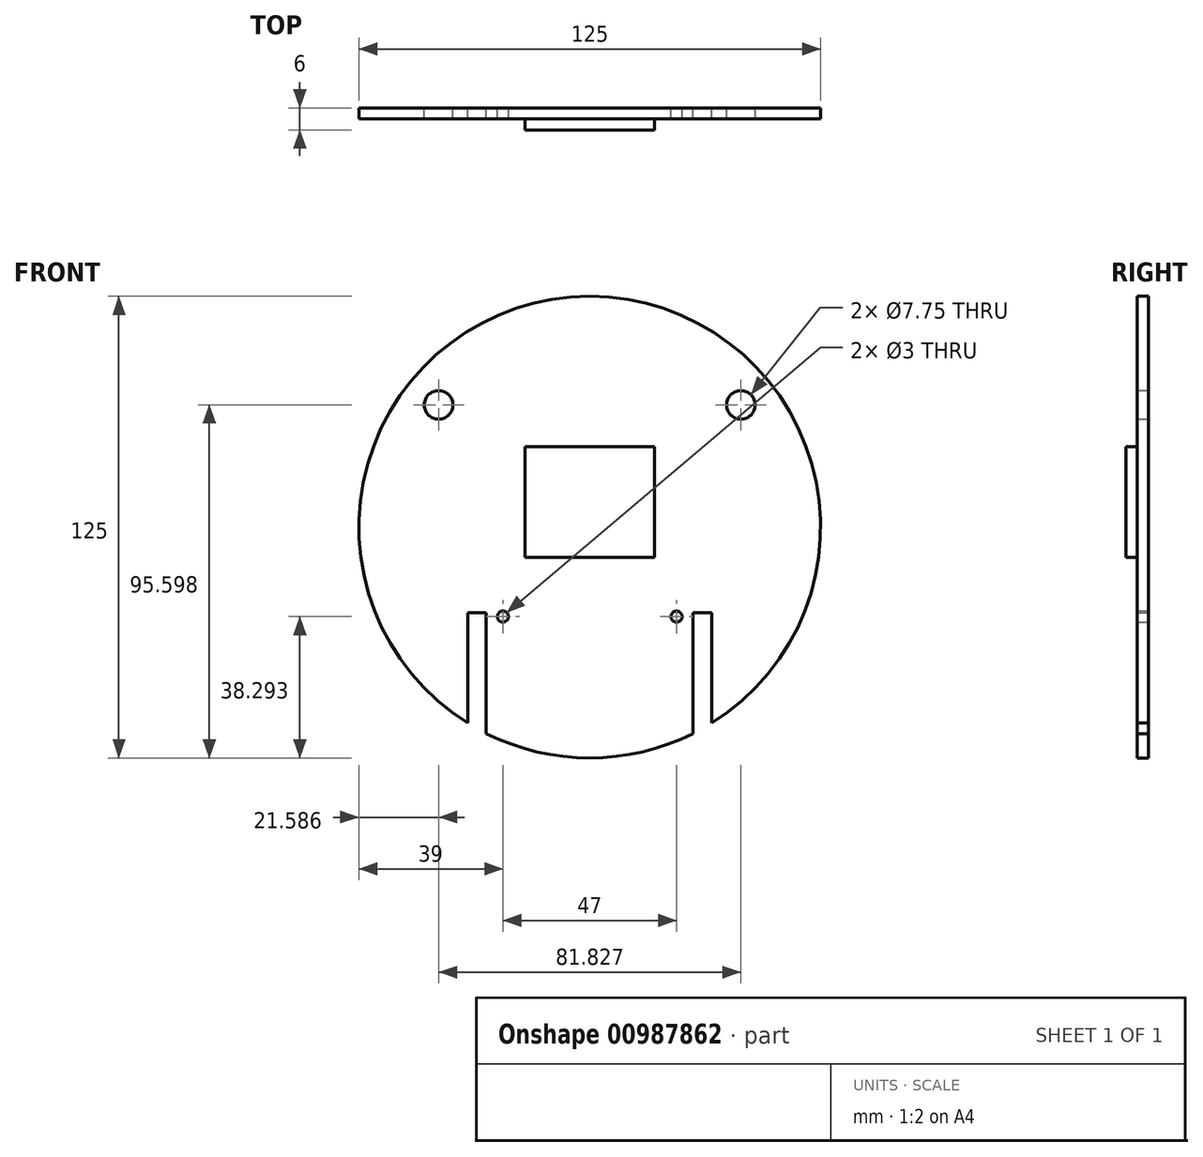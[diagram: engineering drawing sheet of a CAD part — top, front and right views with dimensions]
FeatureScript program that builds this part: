
annotation { "Feature Type Name" : "Feature", "Feature Type Description" : "" }
export const myFeature = defineFeature(function(context is Context, id is Id, definition is map)
    precondition{}
    {
        {
            var Q0;
            Q0=qCreatedBy(makeId("Front.planeOp"),FACE);
            var sketch = newSketch(context, id + "F0", { "sketchPlane" : qUnion([Q0])});
            skCircle(sketch, "E0", {"center": v(0, 0) * mm, "radius": 62.5 * mm});
            skLineSegment(sketch, "E1.bottom", {"start": v(-17.5, -8.2) * mm, "end": v(17.5, -8.2) * mm});
            skLineSegment(sketch, "E1.top", {"start": v(-17.5, 21.8) * mm, "end": v(17.5, 21.8) * mm});
            skLineSegment(sketch, "E1.left", {"start": v(-17.5, -8.2) * mm, "end": v(-17.5, 21.8) * mm});
            skLineSegment(sketch, "E1.right", {"start": v(17.5, -8.2) * mm, "end": v(17.5, 21.8) * mm});
            skPoint(sketch, "E1.middle", {"position": v(0, 6.8) * mm});
            skCircle(sketch, "E2", {"center": v(-40.91, 33.1) * mm, "radius": 26 * mm, "construction": true});
            skCircle(sketch, "E3", {"center": v(-40.91, 33.1) * mm, "radius": 3.88 * mm});
            skCircle(sketch, "E4", {"center": v(40.91, 33.1) * mm, "radius": 3.88 * mm});
            skCircle(sketch, "E5", {"center": v(40.91, 33.1) * mm, "radius": 26 * mm, "construction": true});
            skLineSegment(sketch, "E6", {"start": v(-42.08, -46.2) * mm, "end": v(42.08, -46.2) * mm, "construction": true});
            skLineSegment(sketch, "E7.bottom", {"start": v(-28, -23.2) * mm, "end": v(-33, -23.2) * mm});
            skLineSegment(sketch, "E7.top", {"start": v(-28, -56.2) * mm, "end": v(-33, -56.2) * mm});
            skLineSegment(sketch, "E7.left", {"start": v(-28, -23.2) * mm, "end": v(-28, -56.2) * mm});
            skLineSegment(sketch, "E7.right", {"start": v(-33, -23.2) * mm, "end": v(-33, -56.2) * mm});
            skPoint(sketch, "E7.middle", {"position": v(-30.5, -39.7) * mm});
            skLineSegment(sketch, "E8.bottom", {"start": v(33, -23.2) * mm, "end": v(28, -23.2) * mm});
            skLineSegment(sketch, "E8.top", {"start": v(33, -56.2) * mm, "end": v(28, -56.2) * mm});
            skLineSegment(sketch, "E8.left", {"start": v(33, -23.2) * mm, "end": v(33, -56.2) * mm});
            skLineSegment(sketch, "E8.right", {"start": v(28, -23.2) * mm, "end": v(28, -56.2) * mm});
            skPoint(sketch, "E8.middle", {"position": v(30.5, -39.7) * mm});
            skCircle(sketch, "E9", {"center": v(-23.5, -24.2) * mm, "radius": 1.5 * mm});
            skCircle(sketch, "E10", {"center": v(23.5, -24.2) * mm, "radius": 1.5 * mm});
            skLineSegment(sketch, "E11", {"start": v(-28, -23.2) * mm, "end": v(28, -23.2) * mm, "construction": true});
            skSolve(sketch);
        }
        {
            var Q0;
            Q0=makeQuery(id+"F0.imprint","IMPRINT",FACE,{"disambiguationData":[TD([[makeQuery(id+"F0.imprint","IMPRINT",EDGE,{"derivedFrom":sQuery(id+"F0.wireOp",EDGE,"E1.bottom")}),-1.0]])]});
            var Q1;
            Q1=makeQuery(id+"F0.imprint","IMPRINT",FACE,{"disambiguationData":[TD([[makeQuery(id+"F0.imprint","IMPRINT",EDGE,{"derivedFrom":sQuery(id+"F0.wireOp",EDGE,"E1.bottom")}),1.0]])]});
            extrude(context, id + "F1", {"entities" : qUnion([Q0, Q1]), "depth" : 3 * mm, "offsetDistance" : 25 * mm});
        }
        {
            var Q0;
            Q0=makeQuery(id+"F0.imprint","IMPRINT",FACE,{"disambiguationData":[TD([[makeQuery(id+"F0.imprint","IMPRINT",EDGE,{"derivedFrom":sQuery(id+"F0.wireOp",EDGE,"E1.bottom")}),1.0]])]});
            extrude(context, id + "F2", {"entities" : qUnion([Q0]), "operationType" : NewBodyOperationType.ADD, "depth" : 6 * mm, "offsetDistance" : 25 * mm});
        }
    });
